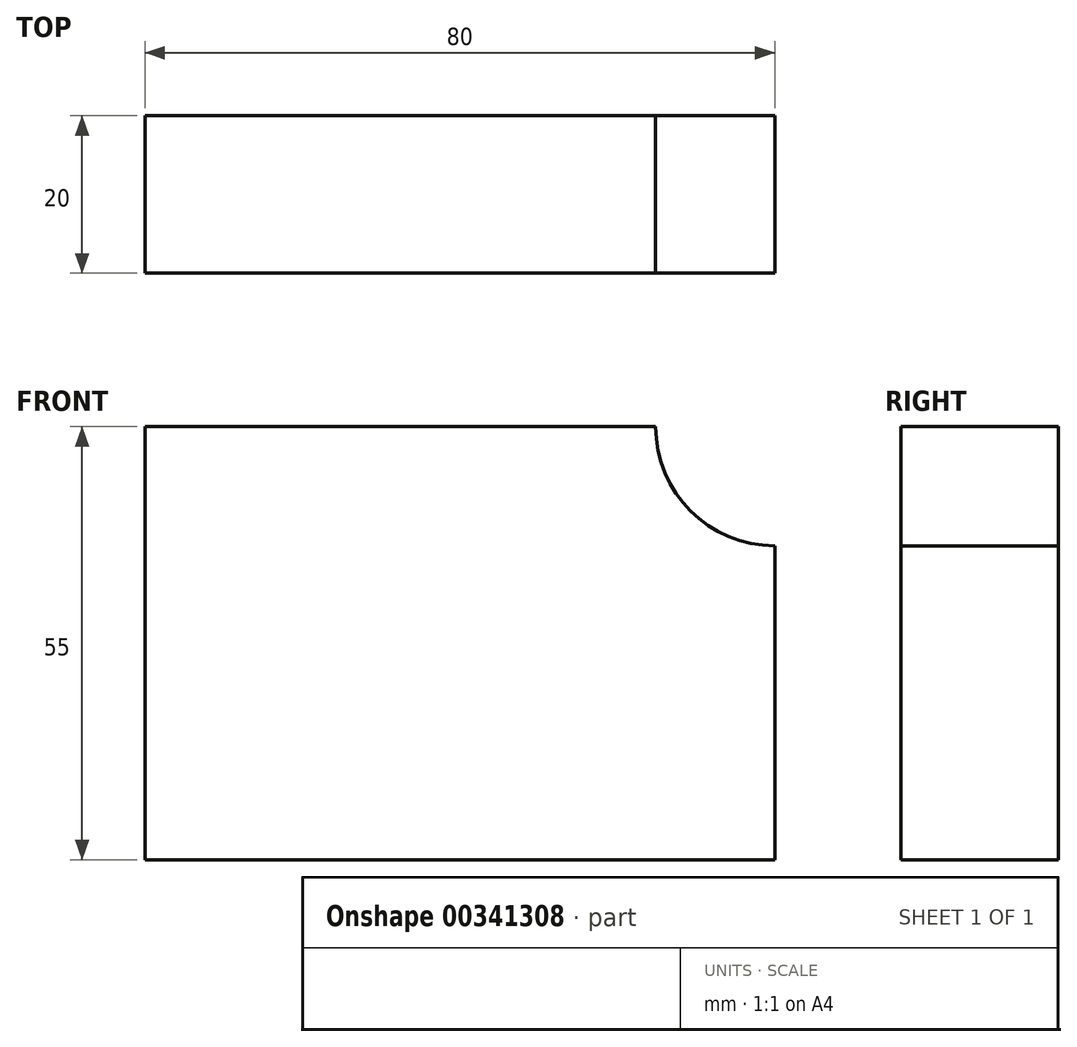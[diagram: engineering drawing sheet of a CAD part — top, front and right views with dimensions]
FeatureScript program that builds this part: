
annotation { "Feature Type Name" : "Feature", "Feature Type Description" : "" }
export const myFeature = defineFeature(function(context is Context, id is Id, definition is map)
    precondition{}
    {
        {
            var Q0;
            Q0=qCreatedBy(makeId("Front.planeOp"),FACE);
            var sketch = newSketch(context, id + "F0", { "sketchPlane" : qUnion([Q0])});
            skLineSegment(sketch, "E0.bottom", {"start": v(0, 0) * mm, "end": v(188, 0) * mm});
            skLineSegment(sketch, "E0.top", {"start": v(0, 188) * mm, "end": v(188, 188) * mm});
            skLineSegment(sketch, "E0.left", {"start": v(0, 0) * mm, "end": v(0, 188) * mm});
            skLineSegment(sketch, "E0.right", {"start": v(188, 0) * mm, "end": v(188, 188) * mm});
            skLineSegment(sketch, "E1", {"start": v(0, 188) * mm, "end": v(48, 188) * mm});
            skLineSegment(sketch, "E2", {"start": v(48, 188) * mm, "end": v(188, 48) * mm});
            skLineSegment(sketch, "E3", {"start": v(188, 48) * mm, "end": v(188, 0) * mm});
            skLineSegment(sketch, "E4.bottom", {"start": v(0, 0) * mm, "end": v(80, 0) * mm});
            skLineSegment(sketch, "E4.top", {"start": v(0, 55) * mm, "end": v(80, 55) * mm});
            skLineSegment(sketch, "E4.left", {"start": v(0, 0) * mm, "end": v(0, 55) * mm});
            skLineSegment(sketch, "E4.right", {"start": v(80, 0) * mm, "end": v(80, 55) * mm});
            skCircle(sketch, "E5", {"center": v(80, 55) * mm, "radius": 15.12 * mm});
            skSolve(sketch);
        }
        {
            var Q0;
            Q0=makeQuery(id+"F0.imprint","IMPRINT",FACE,{"disambiguationData":[TD([[makeQuery(id+"F0.imprint","IMPRINT",EDGE,{"derivedFrom":sQuery(id+"F0.wireOp",EDGE,"E0.bottom")}),1.0]])]});
            var Q1;
            {var subQ1=sQuery(id+"F0.wireOp",EDGE,"E4.bottom");Q1=makeQuery(id+"F0.imprint","IMPRINT",FACE,{"disambiguationData":[TD([[makeQuery(id+"F0.imprint","IMPRINT",EDGE,{"derivedFrom":subQ1}),1.0]])]});}
            extrude(context, id + "F1", {"entities" : qUnion([Q0, Q1]), "depth" : 20 * mm});
        }
    });
